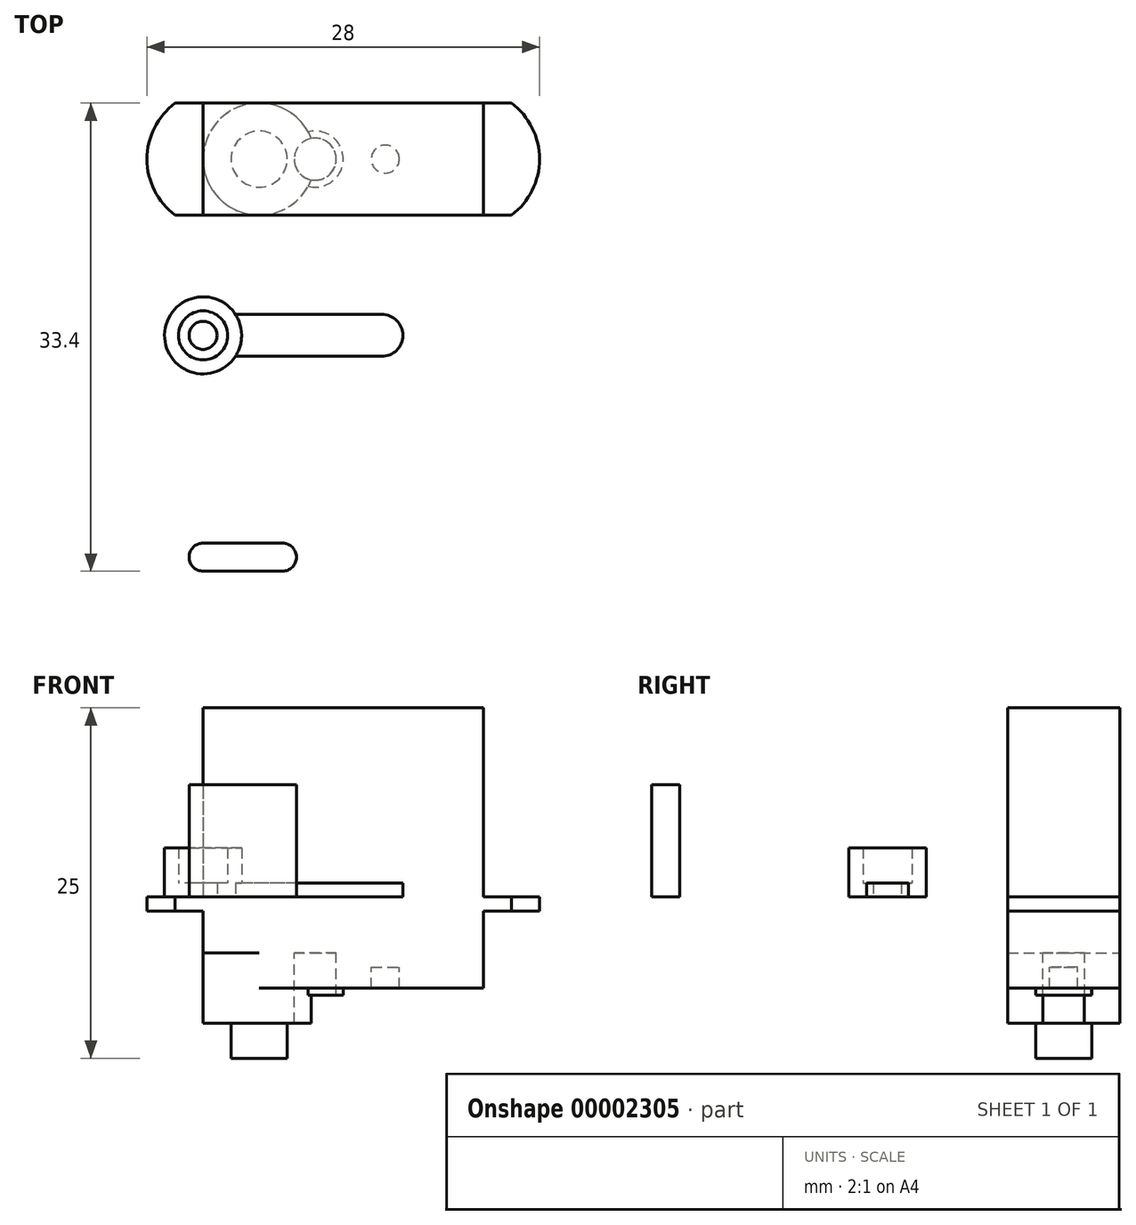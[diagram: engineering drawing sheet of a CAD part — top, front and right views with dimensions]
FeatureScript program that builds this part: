
annotation { "Feature Type Name" : "Feature", "Feature Type Description" : "" }
export const myFeature = defineFeature(function(context is Context, id is Id, definition is map)
    precondition{}
    {
        {
            var Q0;
            Q0=qCreatedBy(makeId("Top.planeOp"),FACE);
            var sketch = newSketch(context, id + "F0", { "sketchPlane" : qUnion([Q0])});
            skLineSegment(sketch, "E0.bottom", {"start": v(0, 0) * mm, "end": v(20, 0) * mm});
            skLineSegment(sketch, "E0.top", {"start": v(0, 8) * mm, "end": v(20, 8) * mm});
            skLineSegment(sketch, "E0.left", {"start": v(0, 0) * mm, "end": v(0, 8) * mm});
            skLineSegment(sketch, "E0.right", {"start": v(20, 0) * mm, "end": v(20, 8) * mm});
            skLineSegment(sketch, "E1", {"start": v(0, 8) * mm, "end": v(-2, 8) * mm});
            skLineSegment(sketch, "E2", {"start": v(0, 0) * mm, "end": v(-2, 0) * mm});
            skArc(sketch, "E3", {"start": v(-2, 8) * mm, "mid": v(-4, 4) * mm, "end": v(-2, 0) * mm});
            skPoint(sketch, "E4", {"position": v(-4, 4) * mm});
            skPoint(sketch, "E5", {"position": v(10, 8) * mm});
            skPoint(sketch, "E6", {"position": v(10, 0) * mm});
            skLineSegment(sketch, "E7", {"start": v(10, 8) * mm, "end": v(10, 0) * mm, "construction": true});
            skLineSegment(sketch, "E8.0.MirrorCS", {"start": v(20, 8) * mm, "end": v(22, 8) * mm});
            skArc(sketch, "E9.0.MirrorCS", {"start": v(22, 8) * mm, "mid": v(24, 4) * mm, "end": v(22, 0) * mm});
            skLineSegment(sketch, "E10.0.MirrorCS", {"start": v(20, 0) * mm, "end": v(22, 0) * mm});
            skSolve(sketch);
        }
        {
            var Q0;
            Q0=makeQuery(id+"F0.imprint","IMPRINT",FACE,{"disambiguationData":[TD([[makeQuery(id+"F0.imprint","IMPRINT",EDGE,{"derivedFrom":sQuery(id+"F0.wireOp",EDGE,"E0.bottom")}),1.0]])]});
            extrude(context, id + "F1", {"entities" : qUnion([Q0]), "depth" : 13.5 * mm});
        }
        {
            var Q0;
            Q0=makeQuery(id+"F0.imprint","IMPRINT",FACE,{"disambiguationData":[TD([[makeQuery(id+"F0.imprint","IMPRINT",EDGE,{"derivedFrom":sQuery(id+"F0.wireOp",EDGE,"E0.bottom")}),1.0]])]});
            extrude(context, id + "F2", {"entities" : qUnion([Q0]), "operationType" : NewBodyOperationType.ADD, "oppositeDirection" : true, "depth" : 4 * mm});
        }
        {
            var Q0;
            Q0=makeQuery(id+"F0.imprint","IMPRINT",FACE,{"disambiguationData":[TD([[makeQuery(id+"F0.imprint","IMPRINT",EDGE,{"derivedFrom":sQuery(id+"F0.wireOp",EDGE,"E0.left")}),1.0]])]});
            var Q1;
            Q1=makeQuery(id+"F0.imprint","IMPRINT",FACE,{"disambiguationData":[TD([[makeQuery(id+"F0.imprint","IMPRINT",EDGE,{"derivedFrom":sQuery(id+"F0.wireOp",EDGE,"E0.right")}),-1.0]])]});
            extrude(context, id + "F3", {"entities" : qUnion([Q0, Q1]), "operationType" : NewBodyOperationType.ADD, "oppositeDirection" : true, "depth" : 1 * mm});
        }
        {
            var Q0;
            Q0=makeQuery(id+"F2.opExtrude","CAP_FACE",FACE,{"disambiguationData":[OSD([sQuery(id+"F0.wireOp",EDGE,"E0.bottom"),sQuery(id+"F0.wireOp",EDGE,"E0.top"),sQuery(id+"F0.wireOp",EDGE,"E0.left"),sQuery(id+"F0.wireOp",EDGE,"E0.right")])],"isStart":false});
            var sketch = newSketch(context, id + "F4", { "sketchPlane" : qUnion([Q0])});
            skCircle(sketch, "E11", {"center": v(4, -4) * mm, "radius": 4 * mm});
            skCircle(sketch, "E12", {"center": v(8, -4) * mm, "radius": 2 * mm});
            skPoint(sketch, "E13", {"position": v(0, -4) * mm});
            skCircle(sketch, "E14.0", {"center": v(8, -4) * mm, "radius": 1.5 * mm});
            skCircle(sketch, "E15", {"center": v(13, -4) * mm, "radius": 1 * mm});
            skCircle(sketch, "E16.0", {"center": v(4, -4) * mm, "radius": 2 * mm});
            skSolve(sketch);
        }
        {
            var Q0;
            {var subQ3=sQuery(id+"F4.wireOp",EDGE,"E16.0");Q0=makeQuery(id+"F4.imprint","IMPRINT",FACE,{"disambiguationData":[TD([[makeQuery(id+"F4.imprint","IMPRINT",EDGE,{"derivedFrom":subQ3}),-1.0]])]});}
            var Q1;
            {var subQ0=sQuery(id+"F4.wireOp",EDGE,"E14.0");var subQ1=sQuery(id+"F4.wireOp",EDGE,"E11");var subQ3=makeQuery(id+"F4.imprint","INTERSECT",VERTEX,{"disambiguationData":[OD(0.0)],"derivedFrom":[subQ1,subQ0]});Q1=makeQuery(id+"F4.imprint","IMPRINT",FACE,{"disambiguationData":[TD([[makeQuery(id+"F4.imprint","IMPRINT",EDGE,{"disambiguationData":[TD([[subQ3,1.0]])],"derivedFrom":subQ1}),1.0]])]});}
            var Q2;
            {var subQ1=sQuery(id+"F4.wireOp",EDGE,"E11");var subQ4=sQuery(id+"F4.wireOp",EDGE,"E12");var subQ7=makeQuery(id+"F4.imprint","INTERSECT",VERTEX,{"disambiguationData":[OD(0.0)],"derivedFrom":[subQ1,subQ4]});Q2=makeQuery(id+"F4.imprint","IMPRINT",FACE,{"disambiguationData":[TD([[makeQuery(id+"F4.imprint","IMPRINT",EDGE,{"disambiguationData":[TD([[subQ7,1.0]])],"derivedFrom":subQ1}),1.0]])]});}
            extrude(context, id + "F5", {"entities" : qUnion([Q0, Q1, Q2]), "operationType" : NewBodyOperationType.ADD, "depth" : 5 * mm});
        }
        {
            var Q0;
            Q0=makeQuery(id+"F4.imprint","IMPRINT",FACE,{"disambiguationData":[TD([[makeQuery(id+"F4.imprint","IMPRINT",EDGE,{"derivedFrom":sQuery(id+"F4.wireOp",EDGE,"E16.0")}),1.0]])]});
            extrude(context, id + "F6", {"entities" : qUnion([Q0]), "operationType" : NewBodyOperationType.ADD, "depth" : 7.5 * mm});
        }
        {
            var Q0;
            {var subQ1=sQuery(id+"F4.wireOp",EDGE,"E11");var subQ4=sQuery(id+"F4.wireOp",EDGE,"E12");var subQ6=makeQuery(id+"F4.imprint","INTERSECT",VERTEX,{"disambiguationData":[OD(0.0)],"derivedFrom":[subQ1,subQ4]});Q0=makeQuery(id+"F4.imprint","IMPRINT",FACE,{"disambiguationData":[TD([[makeQuery(id+"F4.imprint","IMPRINT",EDGE,{"disambiguationData":[TD([[subQ6,1.0]])],"derivedFrom":subQ1}),-1.0]])]});}
            extrude(context, id + "F7", {"entities" : qUnion([Q0]), "operationType" : NewBodyOperationType.ADD, "depth" : 2.5 * mm});
        }
        {
            var Q0;
            {var subQ0=sQuery(id+"F4.wireOp",EDGE,"E14.0");var subQ1=sQuery(id+"F4.wireOp",EDGE,"E11");var subQ3=makeQuery(id+"F4.imprint","INTERSECT",VERTEX,{"disambiguationData":[OD(0.0)],"derivedFrom":[subQ1,subQ0]});Q0=makeQuery(id+"F4.imprint","IMPRINT",FACE,{"disambiguationData":[TD([[makeQuery(id+"F4.imprint","IMPRINT",EDGE,{"disambiguationData":[TD([[subQ3,1.0]])],"derivedFrom":subQ1}),-1.0]])]});}
            extrude(context, id + "F8", {"entities" : qUnion([Q0]), "operationType" : NewBodyOperationType.ADD, "depth" : 3 * mm});
        }
        {
            var Q0;
            Q0=makeQuery(id+"F4.imprint","IMPRINT",FACE,{"disambiguationData":[TD([[makeQuery(id+"F4.imprint","IMPRINT",EDGE,{"derivedFrom":sQuery(id+"F4.wireOp",EDGE,"E15")}),1.0]])]});
            extrude(context, id + "F9", {"entities" : qUnion([Q0]), "operationType" : NewBodyOperationType.ADD, "depth" : 1 * mm});
        }
        {
            var Q0;
            Q0=makeQuery(id+"F6.opExtrude","CAP_FACE",FACE,{"disambiguationData":[OSD([sQuery(id+"F4.wireOp",EDGE,"E16.0")])],"isStart":false});
            var sketch = newSketch(context, id + "F10", { "sketchPlane" : qUnion([Q0])});
            skPoint(sketch, "E17", {"position": v(4, -4) * mm});
            skSolve(sketch);
        }
        {
            var Q0;
            Q0=qCreatedBy(makeId("Top.planeOp"),FACE);
            var sketch = newSketch(context, id + "F11", { "sketchPlane" : qUnion([Q0])});
            skCircle(sketch, "E18", {"center": v(0, -8.57) * mm, "radius": 2.75 * mm});
            skLineSegment(sketch, "E19", {"start": v(0, -8.57) * mm, "end": v(12.75, -8.57) * mm, "construction": true});
            skCircle(sketch, "E20", {"center": v(12.75, -8.57) * mm, "radius": 1.5 * mm});
            skLineSegment(sketch, "E21", {"start": v(12.75, -7.07) * mm, "end": v(2.3, -7.07) * mm});
            skLineSegment(sketch, "E22", {"start": v(12.75, -10.07) * mm, "end": v(2.3, -10.07) * mm});
            skCircle(sketch, "E23.0", {"center": v(0, -8.57) * mm, "radius": 1.75 * mm});
            skCircle(sketch, "E24", {"center": v(0, -8.57) * mm, "radius": 1 * mm});
            skCircle(sketch, "E25", {"center": v(0, -24.4) * mm, "radius": 1 * mm});
            skCircle(sketch, "E26", {"center": v(5.66, -24.4) * mm, "radius": 1 * mm});
            skLineSegment(sketch, "E27", {"start": v(0, -23.4) * mm, "end": v(5.66, -23.4) * mm});
            skLineSegment(sketch, "E28", {"start": v(0, -25.4) * mm, "end": v(5.66, -25.4) * mm});
            skSolve(sketch);
        }
        {
            var Q0;
            Q0=makeQuery(id+"F11.imprint","IMPRINT",FACE,{"disambiguationData":[TD([[makeQuery(id+"F11.imprint","IMPRINT",EDGE,{"derivedFrom":sQuery(id+"F11.wireOp",EDGE,"E23.0")}),-1.0]])]});
            extrude(context, id + "F12", {"entities" : qUnion([Q0]), "depth" : 3.5 * mm});
        }
        {
            var Q0;
            {var subQ1=sQuery(id+"F11.wireOp",EDGE,"E21");Q0=makeQuery(id+"F11.imprint","IMPRINT",FACE,{"disambiguationData":[TD([[makeQuery(id+"F11.imprint","IMPRINT",EDGE,{"derivedFrom":subQ1}),1.0]])]});}
            var Q1;
            {var subQ0=sQuery(id+"F11.wireOp",EDGE,"E20");var subQ2=makeQuery(id+"F11.imprint","INTERSECT",VERTEX,{"derivedFrom":[subQ0,sQuery(id+"F11.wireOp",EDGE,"E21")]});Q1=makeQuery(id+"F11.imprint","IMPRINT",FACE,{"disambiguationData":[TD([[makeQuery(id+"F11.imprint","IMPRINT",EDGE,{"disambiguationData":[TD([[subQ2,-1.0]])],"derivedFrom":subQ0}),1.0]])]});}
            extrude(context, id + "F13", {"entities" : qUnion([Q0, Q1]), "operationType" : NewBodyOperationType.ADD, "depth" : 1 * mm});
        }
        {
            var Q0;
            Q0=makeQuery(id+"F11.imprint","IMPRINT",FACE,{"disambiguationData":[TD([[makeQuery(id+"F11.imprint","IMPRINT",EDGE,{"derivedFrom":sQuery(id+"F11.wireOp",EDGE,"E23.0")}),1.0]])]});
            extrude(context, id + "F14", {"entities" : qUnion([Q0]), "operationType" : NewBodyOperationType.ADD, "depth" : 1 * mm});
        }
        {
            var Q0;
            {var subQ0=sQuery(id+"F11.wireOp",EDGE,"E25");var subQ2=makeQuery(id+"F11.imprint","INTERSECT",VERTEX,{"derivedFrom":[subQ0,sQuery(id+"F11.wireOp",EDGE,"E27")]});Q0=makeQuery(id+"F11.imprint","IMPRINT",FACE,{"disambiguationData":[TD([[makeQuery(id+"F11.imprint","IMPRINT",EDGE,{"disambiguationData":[TD([[subQ2,-1.0]])],"derivedFrom":subQ0}),1.0]])]});}
            var Q1;
            {var subQ1=sQuery(id+"F11.wireOp",EDGE,"E27");Q1=makeQuery(id+"F11.imprint","IMPRINT",FACE,{"disambiguationData":[TD([[makeQuery(id+"F11.imprint","IMPRINT",EDGE,{"derivedFrom":subQ1}),-1.0]])]});}
            var Q2;
            {var subQ0=sQuery(id+"F11.wireOp",EDGE,"E26");var subQ2=makeQuery(id+"F11.imprint","INTERSECT",VERTEX,{"derivedFrom":[subQ0,sQuery(id+"F11.wireOp",EDGE,"E27")]});Q2=makeQuery(id+"F11.imprint","IMPRINT",FACE,{"disambiguationData":[TD([[makeQuery(id+"F11.imprint","IMPRINT",EDGE,{"disambiguationData":[TD([[subQ2,-1.0]])],"derivedFrom":subQ0}),1.0]])]});}
            extrude(context, id + "F15", {"entities" : qUnion([Q0, Q1, Q2]), "depth" : 8 * mm});
        }
    });
